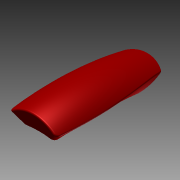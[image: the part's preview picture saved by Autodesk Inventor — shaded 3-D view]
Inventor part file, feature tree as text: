
AUTODESK INVENTOR PART (.ipt)
format: ipt  version: 2011 (Build 150239000, 239)  size: 439,808 bytes
history: native  units: mm (DEFAULTED — no unit token found)
features: other x2, split x1, extrude x1, fillet x1, sketch x1, imported_body x1
ambient origin geometry x8: Origin, YZ Plane, XZ Plane, XY Plane, X Axis, Y Axis, Z Axis, Center Point
bodies: Solid1 (feature_tree)
feature tree (7):
  other  "Upper - Master.ipt"
  split  "Split1"
  extrude  "Extrusion1"  Depth=25.4mm
  fillet  "Fillet1"  Radius=101.6mm
  other  "Slice"
  sketch  "Sketch3"  dims[d1=10.0mm d4=25.4mm d5=101.6mm d6=25.4mm d7=0.0mm d8=3.175mm]
  imported_body  "DerivedBody::Upper - Master.ipt"
